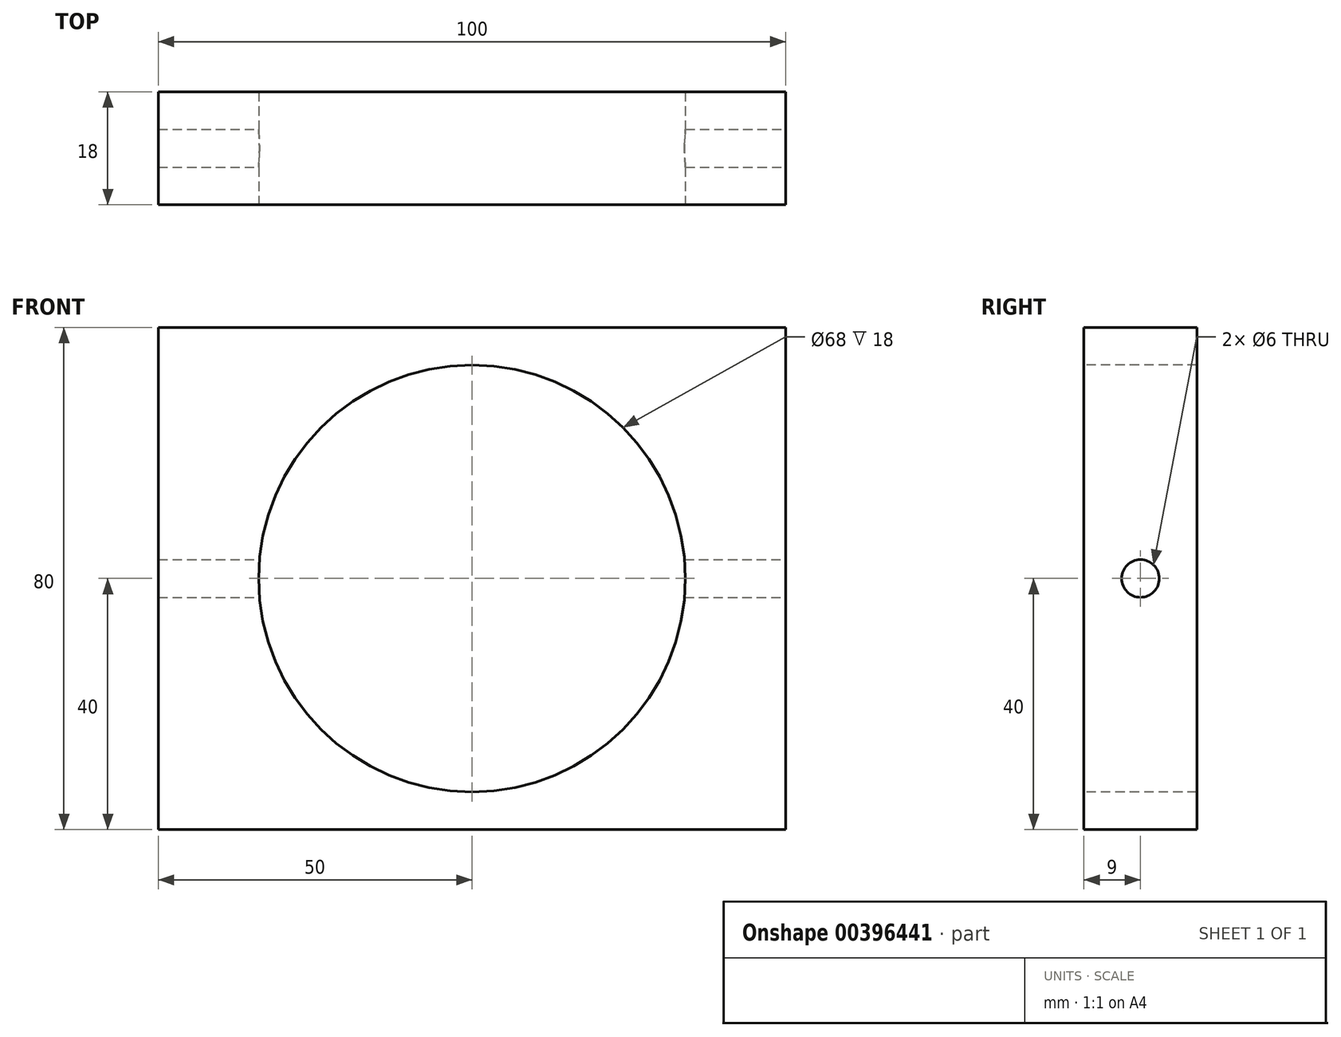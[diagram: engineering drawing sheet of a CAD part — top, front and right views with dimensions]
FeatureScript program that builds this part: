
annotation { "Feature Type Name" : "Feature", "Feature Type Description" : "" }
export const myFeature = defineFeature(function(context is Context, id is Id, definition is map)
    precondition{}
    {
        {
            var Q0;
            Q0=qCreatedBy(makeId("Front.planeOp"),FACE);
            var sketch = newSketch(context, id + "F0", { "sketchPlane" : qUnion([Q0])});
            skLineSegment(sketch, "E0.bottom", {"start": v(0, 0) * mm, "end": v(100, 0) * mm});
            skLineSegment(sketch, "E0.top", {"start": v(0, 80) * mm, "end": v(100, 80) * mm});
            skLineSegment(sketch, "E0.left", {"start": v(0, 0) * mm, "end": v(0, 80) * mm});
            skLineSegment(sketch, "E0.right", {"start": v(100, 0) * mm, "end": v(100, 80) * mm});
            skSolve(sketch);
        }
        {
            var Q0;
            Q0 = qSketchRegion(id + "F0", true);
            extrude(context, id + "F1", {"entities" : qUnion([Q0]), "depth" : 18 * mm});
        }
        {
            var Q0;
            Q0=makeQuery(id+"F1.opExtrude","CAP_FACE",FACE,{"disambiguationData":[OSD([sQuery(id+"F0.wireOp",EDGE,"E0.bottom"),sQuery(id+"F0.wireOp",EDGE,"E0.top"),sQuery(id+"F0.wireOp",EDGE,"E0.left"),sQuery(id+"F0.wireOp",EDGE,"E0.right")])],"isStart":false});
            var sketch = newSketch(context, id + "F2", { "sketchPlane" : qUnion([Q0])});
            skPoint(sketch, "E1", {"position": v(50, 40) * mm});
            skSolve(sketch);
        }
        {
            var Q0;
            Q0=sQuery(id+"F2.wireOp",VERTEX,"E1");
            var Q1;
            Q1=makeQuery(id+"F1.opExtrude","SWEPT_BODY",BODY,{"disambiguationData":[OSD([sQuery(id+"F0.wireOp",EDGE,"E0.bottom"),sQuery(id+"F0.wireOp",EDGE,"E0.top"),sQuery(id+"F0.wireOp",EDGE,"E0.left"),sQuery(id+"F0.wireOp",EDGE,"E0.right")])]});
            hole(context, id + "F3", {"style" : HoleStyle.SIMPLE, "endStyle" : HoleEndStyle.THROUGH, "holeDiameter" : 68 * mm, "isTappedThrough" : true, "tappedDepth" : 12 * mm, "tapClearance" : 3, "locations" : qUnion([Q0]), "scope" : qUnion([Q1])});
        }
        {
            var Q0;
            Q0=makeQuery(id+"F1.opExtrude","SWEPT_FACE",FACE,{"disambiguationData":[OSD([sQuery(id+"F0.wireOp",EDGE,"E0.right")])]});
            var sketch = newSketch(context, id + "F4", { "sketchPlane" : qUnion([Q0])});
            skPoint(sketch, "E2", {"position": v(-9, 40) * mm});
            skSolve(sketch);
        }
        {
            var Q0;
            Q0=sQuery(id+"F4.wireOp",VERTEX,"E2");
            var Q1;
            Q1=makeQuery(id+"F1.opExtrude","SWEPT_BODY",BODY,{"disambiguationData":[OSD([sQuery(id+"F0.wireOp",EDGE,"E0.bottom"),sQuery(id+"F0.wireOp",EDGE,"E0.top"),sQuery(id+"F0.wireOp",EDGE,"E0.left"),sQuery(id+"F0.wireOp",EDGE,"E0.right")])]});
            hole(context, id + "F5", {"style" : HoleStyle.SIMPLE, "endStyle" : HoleEndStyle.THROUGH, "holeDiameter" : 6 * mm, "isTappedThrough" : true, "tappedDepth" : 12 * mm, "tapClearance" : 3, "locations" : qUnion([Q0]), "scope" : qUnion([Q1])});
        }
    });
